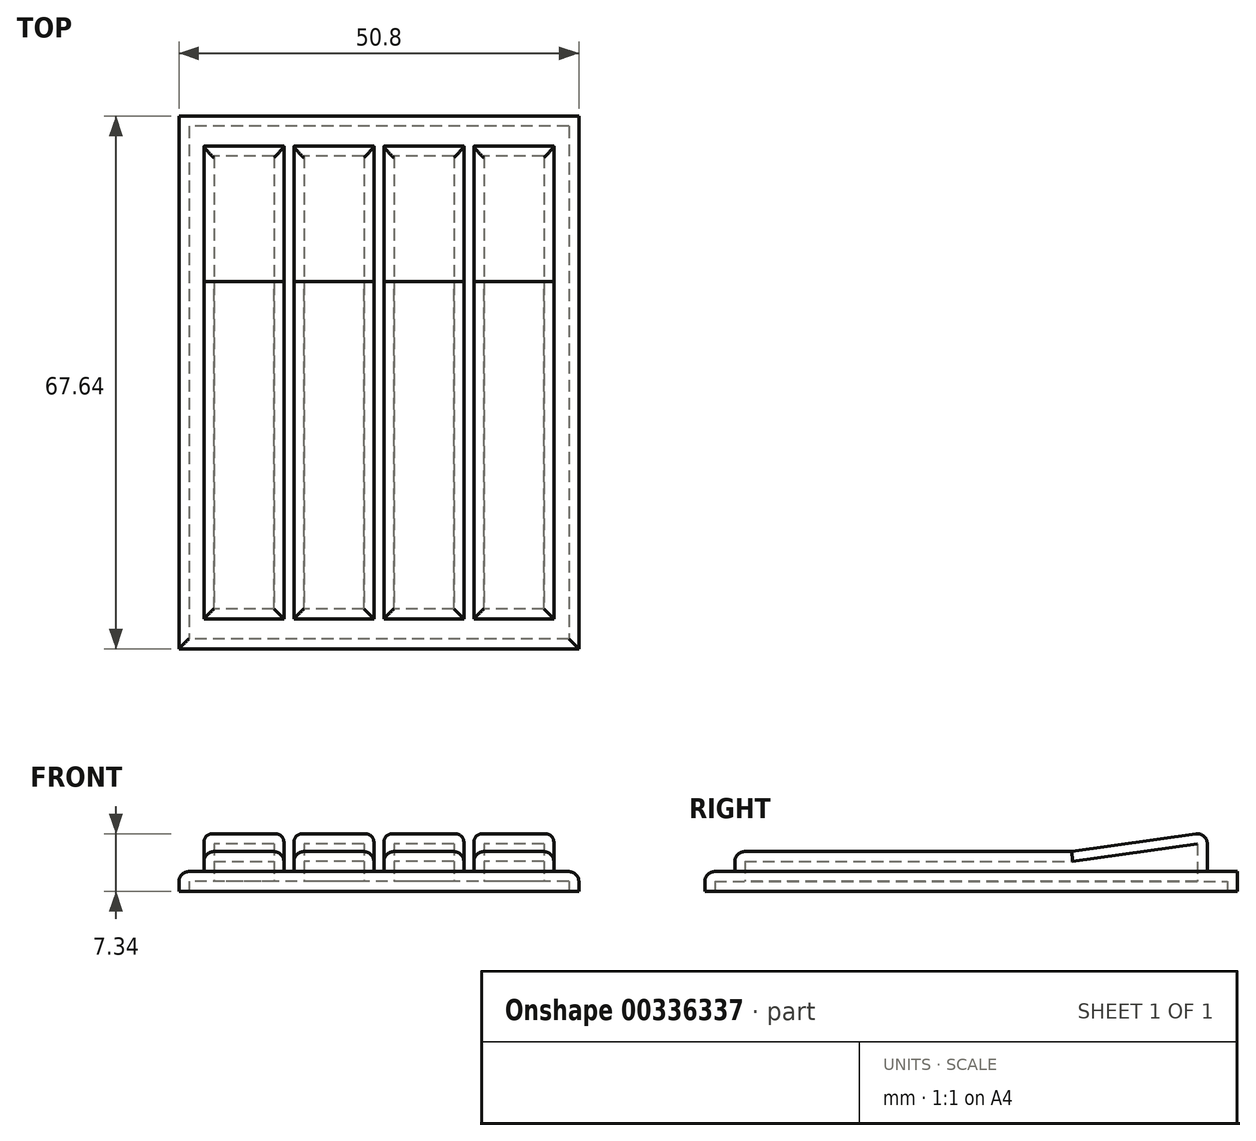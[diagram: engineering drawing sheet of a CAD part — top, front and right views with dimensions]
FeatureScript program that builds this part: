
annotation { "Feature Type Name" : "Feature", "Feature Type Description" : "" }
export const myFeature = defineFeature(function(context is Context, id is Id, definition is map)
    precondition{}
    {
        {
            var Q0;
            Q0=qCreatedBy(makeId("Top.planeOp"),FACE);
            var sketch = newSketch(context, id + "F0", { "sketchPlane" : qUnion([Q0])});
            skPoint(sketch, "E0.visualSharp", {"position": v(-51.01, 40.39) * mm});
            skPoint(sketch, "E1.visualSharp", {"position": v(51.07, 40.48) * mm});
            skPoint(sketch, "E2.visualSharp", {"position": v(0.11, -47.97) * mm});
            skLineSegment(sketch, "E3.bottom", {"start": v(25.4, 33.82) * mm, "end": v(-25.4, 33.82) * mm});
            skLineSegment(sketch, "E3.top", {"start": v(25.4, -33.82) * mm, "end": v(-25.4, -33.82) * mm});
            skLineSegment(sketch, "E3.left", {"start": v(25.4, 33.82) * mm, "end": v(25.4, -33.82) * mm});
            skLineSegment(sketch, "E3.right", {"start": v(-25.4, 33.82) * mm, "end": v(-25.4, -33.82) * mm});
            skPoint(sketch, "E3.middle", {"position": v(-17.14, 0) * mm});
            skLineSegment(sketch, "E4.bottom", {"start": v(-12.06, 30) * mm, "end": v(-22.22, 30) * mm});
            skLineSegment(sketch, "E4.top", {"start": v(-12.06, -30) * mm, "end": v(-22.22, -30) * mm});
            skLineSegment(sketch, "E4.left", {"start": v(-12.06, 30) * mm, "end": v(-12.06, -30) * mm});
            skLineSegment(sketch, "E4.right", {"start": v(-22.22, 30) * mm, "end": v(-22.22, -30) * mm});
            skPoint(sketch, "E5.1.0.0", {"position": v(-5.71, 0) * mm});
            skLineSegment(sketch, "E5.1.0.1", {"start": v(-0.63, -30) * mm, "end": v(-10.8, -30) * mm});
            skLineSegment(sketch, "E5.1.0.2", {"start": v(-0.63, 30) * mm, "end": v(-0.63, -30) * mm});
            skLineSegment(sketch, "E5.1.0.3", {"start": v(-10.8, 30) * mm, "end": v(-10.8, -30) * mm});
            skLineSegment(sketch, "E5.1.0.4", {"start": v(-0.63, 30) * mm, "end": v(-10.8, 30) * mm});
            skPoint(sketch, "E5.1.0.5", {"position": v(-5.71, 0) * mm});
            skPoint(sketch, "E5.2.0.0", {"position": v(5.72, 0) * mm});
            skLineSegment(sketch, "E5.2.0.1", {"start": v(10.8, -30) * mm, "end": v(0.64, -30) * mm});
            skLineSegment(sketch, "E5.2.0.2", {"start": v(10.8, 30) * mm, "end": v(10.8, -30) * mm});
            skLineSegment(sketch, "E5.2.0.3", {"start": v(0.64, 30) * mm, "end": v(0.64, -30) * mm});
            skLineSegment(sketch, "E5.2.0.4", {"start": v(10.8, 30) * mm, "end": v(0.64, 30) * mm});
            skPoint(sketch, "E5.2.0.5", {"position": v(5.72, 0) * mm});
            skPoint(sketch, "E5.3.0.0", {"position": v(17.15, 0) * mm});
            skLineSegment(sketch, "E5.3.0.1", {"start": v(22.23, -30) * mm, "end": v(12.07, -30) * mm});
            skLineSegment(sketch, "E5.3.0.2", {"start": v(22.23, 30) * mm, "end": v(22.23, -30) * mm});
            skLineSegment(sketch, "E5.3.0.3", {"start": v(12.07, 30) * mm, "end": v(12.07, -30) * mm});
            skLineSegment(sketch, "E5.3.0.4", {"start": v(22.23, 30) * mm, "end": v(12.07, 30) * mm});
            skPoint(sketch, "E5.3.0.5", {"position": v(17.15, 0) * mm});
            skLineSegment(sketch, "E5.direction1", {"start": v(-22.22, -30) * mm, "end": v(-10.8, -30) * mm, "construction": true});
            skLineSegment(sketch, "E6", {"start": v(-22.22, 12.8) * mm, "end": v(22.23, 12.8) * mm});
            skSolve(sketch);
        }
        {
            var Q0;
            {var subQ0=sQuery(id+"F0.wireOp",EDGE,"E4.bottom");Q0=makeQuery(id+"F0.imprint","IMPRINT",FACE,{"disambiguationData":[TD([[makeQuery(id+"F0.imprint","IMPRINT",EDGE,{"derivedFrom":subQ0}),1.0]])]});}
            var Q1;
            {var subQ0=sQuery(id+"F0.wireOp",EDGE,"E5.1.0.4");Q1=makeQuery(id+"F0.imprint","IMPRINT",FACE,{"disambiguationData":[TD([[makeQuery(id+"F0.imprint","IMPRINT",EDGE,{"derivedFrom":subQ0}),1.0]])]});}
            var Q2;
            {var subQ0=sQuery(id+"F0.wireOp",EDGE,"E5.2.0.4");Q2=makeQuery(id+"F0.imprint","IMPRINT",FACE,{"disambiguationData":[TD([[makeQuery(id+"F0.imprint","IMPRINT",EDGE,{"derivedFrom":subQ0}),1.0]])]});}
            var Q3;
            {var subQ0=sQuery(id+"F0.wireOp",EDGE,"E5.3.0.4");Q3=makeQuery(id+"F0.imprint","IMPRINT",FACE,{"disambiguationData":[TD([[makeQuery(id+"F0.imprint","IMPRINT",EDGE,{"derivedFrom":subQ0}),1.0]])]});}
            extrude(context, id + "F1", {"entities" : qUnion([Q0, Q1, Q2, Q3]), "depth" : 7.62 * mm});
        }
        {
            var Q0;
            Q0=makeQuery(id+"F0.imprint","IMPRINT",FACE,{"disambiguationData":[TD([[makeQuery(id+"F0.imprint","IMPRINT",EDGE,{"derivedFrom":sQuery(id+"F0.wireOp",EDGE,"E4.bottom")}),1.0]])]});
            var Q1;
            Q1=makeQuery(id+"F0.imprint","IMPRINT",FACE,{"disambiguationData":[TD([[makeQuery(id+"F0.imprint","IMPRINT",EDGE,{"derivedFrom":sQuery(id+"F0.wireOp",EDGE,"E5.1.0.1")}),-1.0]])]});
            var Q2;
            Q2=makeQuery(id+"F0.imprint","IMPRINT",FACE,{"disambiguationData":[TD([[makeQuery(id+"F0.imprint","IMPRINT",EDGE,{"derivedFrom":sQuery(id+"F0.wireOp",EDGE,"E5.2.0.1")}),-1.0]])]});
            var Q3;
            Q3=makeQuery(id+"F0.imprint","IMPRINT",FACE,{"disambiguationData":[TD([[makeQuery(id+"F0.imprint","IMPRINT",EDGE,{"derivedFrom":sQuery(id+"F0.wireOp",EDGE,"E5.3.0.1")}),-1.0]])]});
            var Q4;
            {var subQ0=sQuery(id+"F0.wireOp",EDGE,"E4.top");Q4=makeQuery(id+"F0.imprint","IMPRINT",FACE,{"disambiguationData":[TD([[makeQuery(id+"F0.imprint","IMPRINT",EDGE,{"derivedFrom":subQ0}),-1.0]])]});}
            var Q5;
            {var subQ0=sQuery(id+"F0.wireOp",EDGE,"E5.1.0.4");Q5=makeQuery(id+"F0.imprint","IMPRINT",FACE,{"disambiguationData":[TD([[makeQuery(id+"F0.imprint","IMPRINT",EDGE,{"derivedFrom":subQ0}),1.0]])]});}
            var Q6;
            {var subQ0=sQuery(id+"F0.wireOp",EDGE,"E5.2.0.4");Q6=makeQuery(id+"F0.imprint","IMPRINT",FACE,{"disambiguationData":[TD([[makeQuery(id+"F0.imprint","IMPRINT",EDGE,{"derivedFrom":subQ0}),1.0]])]});}
            var Q7;
            {var subQ0=sQuery(id+"F0.wireOp",EDGE,"E5.3.0.4");Q7=makeQuery(id+"F0.imprint","IMPRINT",FACE,{"disambiguationData":[TD([[makeQuery(id+"F0.imprint","IMPRINT",EDGE,{"derivedFrom":subQ0}),1.0]])]});}
            extrude(context, id + "F2", {"entities" : qUnion([Q0, Q1, Q2, Q3, Q4, Q5, Q6, Q7]), "depth" : 5.08 * mm});
        }
        {
            var Q0;
            Q0 = qSketchRegion(id + "F0", true);
            extrude(context, id + "F3", {"entities" : qUnion([Q0]), "depth" : 2.54 * mm});
        }
        {
            var Q0;
            {var subQ0=sQuery(id+"F0.wireOp",EDGE,"E6");Q0=makeQuery(id+"F1.opExtrude","CAP_EDGE",EDGE,{"disambiguationData":[OSD([subQ0]),TDD([makeQuery(id+"F0.imprint","IMPRINT",EDGE,{"disambiguationData":[TD([[makeQuery(id+"F0.imprint","INTERSECT",VERTEX,{"derivedFrom":[sQuery(id+"F0.wireOp",EDGE,"E4.right"),subQ0]}),-1.0]])],"derivedFrom":subQ0})])],"isStart":false});}
            var Q1;
            {var subQ0=sQuery(id+"F0.wireOp",EDGE,"E6");Q1=makeQuery(id+"F1.opExtrude","CAP_EDGE",EDGE,{"disambiguationData":[OSD([subQ0]),TDD([makeQuery(id+"F0.imprint","IMPRINT",EDGE,{"disambiguationData":[TD([[makeQuery(id+"F0.imprint","INTERSECT",VERTEX,{"derivedFrom":[sQuery(id+"F0.wireOp",EDGE,"E5.1.0.2"),subQ0]}),1.0]])],"derivedFrom":subQ0})])],"isStart":false});}
            var Q2;
            {var subQ0=sQuery(id+"F0.wireOp",EDGE,"E6");Q2=makeQuery(id+"F1.opExtrude","CAP_EDGE",EDGE,{"disambiguationData":[OSD([subQ0]),TDD([makeQuery(id+"F0.imprint","IMPRINT",EDGE,{"disambiguationData":[TD([[makeQuery(id+"F0.imprint","INTERSECT",VERTEX,{"derivedFrom":[sQuery(id+"F0.wireOp",EDGE,"E5.2.0.2"),subQ0]}),1.0]])],"derivedFrom":subQ0})])],"isStart":false});}
            var Q3;
            {var subQ0=sQuery(id+"F0.wireOp",EDGE,"E6");Q3=makeQuery(id+"F1.opExtrude","CAP_EDGE",EDGE,{"disambiguationData":[OSD([subQ0]),TDD([makeQuery(id+"F0.imprint","IMPRINT",EDGE,{"disambiguationData":[TD([[makeQuery(id+"F0.imprint","INTERSECT",VERTEX,{"derivedFrom":[sQuery(id+"F0.wireOp",EDGE,"E5.3.0.2"),subQ0]}),1.0]])],"derivedFrom":subQ0})])],"isStart":false});}
            chamfer(context, id + "F4", {"entities" : qUnion([Q0, Q1, Q2, Q3]), "chamferType" : ChamferType.TWO_OFFSETS, "width1" : 17.78 * mm, "oppositeDirection" : false, "width2" : 2.54 * mm, "tangentPropagation" : true});
        }
        {
            var Q0;
            Q0=makeQuery(id+"F3.opExtrude","CAP_EDGE",EDGE,{"disambiguationData":[OSD([sQuery(id+"F0.wireOp",EDGE,"E3.top")])],"isStart":false});
            var Q1;
            Q1=makeQuery(id+"F3.opExtrude","CAP_EDGE",EDGE,{"disambiguationData":[OSD([sQuery(id+"F0.wireOp",EDGE,"E3.right")])],"isStart":false});
            var Q2;
            Q2=makeQuery(id+"F3.opExtrude","CAP_EDGE",EDGE,{"disambiguationData":[OSD([sQuery(id+"F0.wireOp",EDGE,"E3.left")])],"isStart":false});
            fillet(context, id + "F5", {"entities" : qUnion([Q0, Q1, Q2]), "radius" : 1.27 * mm, "tangentPropagation" : true, "allowEdgeOverflow" : false});
        }
        {
            var Q0;
            Q0=makeQuery(id+"F2.opExtrude","CAP_FACE",FACE,{"disambiguationData":[OSD([sQuery(id+"F0.wireOp",EDGE,"E4.bottom"),sQuery(id+"F0.wireOp",EDGE,"E4.top"),sQuery(id+"F0.wireOp",EDGE,"E4.left"),sQuery(id+"F0.wireOp",EDGE,"E4.right")])],"isStart":false});
            var Q1;
            Q1=makeQuery(id+"F2.opExtrude","CAP_FACE",FACE,{"disambiguationData":[OSD([sQuery(id+"F0.wireOp",EDGE,"E5.1.0.1"),sQuery(id+"F0.wireOp",EDGE,"E5.1.0.2"),sQuery(id+"F0.wireOp",EDGE,"E5.1.0.3"),sQuery(id+"F0.wireOp",EDGE,"E5.1.0.4")])],"isStart":false});
            var Q2;
            Q2=makeQuery(id+"F2.opExtrude","CAP_FACE",FACE,{"disambiguationData":[OSD([sQuery(id+"F0.wireOp",EDGE,"E5.2.0.1"),sQuery(id+"F0.wireOp",EDGE,"E5.2.0.2"),sQuery(id+"F0.wireOp",EDGE,"E5.2.0.3"),sQuery(id+"F0.wireOp",EDGE,"E5.2.0.4")])],"isStart":false});
            var Q3;
            Q3=makeQuery(id+"F2.opExtrude","CAP_FACE",FACE,{"disambiguationData":[OSD([sQuery(id+"F0.wireOp",EDGE,"E5.3.0.1"),sQuery(id+"F0.wireOp",EDGE,"E5.3.0.2"),sQuery(id+"F0.wireOp",EDGE,"E5.3.0.3"),sQuery(id+"F0.wireOp",EDGE,"E5.3.0.4")])],"isStart":false});
            fillet(context, id + "F6", {"entities" : qUnion([Q0, Q1, Q2, Q3]), "radius" : 1.27 * mm, "tangentPropagation" : true, "allowEdgeOverflow" : false});
        }
        {
            var Q0;
            {var subQ0=sQuery(id+"F0.wireOp",EDGE,"E6");Q0=makeQuery(id+"F4.opChamfer","BLEND_EDGE",EDGE,{"blendedFrom":[makeQuery(id+"F1.opExtrude","CAP_EDGE",EDGE,{"disambiguationData":[OSD([subQ0]),TDD([makeQuery(id+"F0.imprint","IMPRINT",EDGE,{"disambiguationData":[TD([[makeQuery(id+"F0.imprint","INTERSECT",VERTEX,{"derivedFrom":[sQuery(id+"F0.wireOp",EDGE,"E4.right"),subQ0]}),-1.0]])],"derivedFrom":subQ0})])],"isStart":false}),makeQuery(id+"F1.opExtrude","SWEPT_FACE",FACE,{"disambiguationData":[OSD([sQuery(id+"F0.wireOp",EDGE,"E4.bottom")])]})],"blendedInto":[makeQuery(id+"F1.opExtrude","SWEPT_FACE",FACE,{"disambiguationData":[OSD([sQuery(id+"F0.wireOp",EDGE,"E4.bottom")])]})]});}
            var Q1;
            {var subQ0=sQuery(id+"F0.wireOp",EDGE,"E4.right");var subQ1=sQuery(id+"F0.wireOp",EDGE,"E6");Q1=makeQuery(id+"F4.opChamfer","BLEND_EDGE",EDGE,{"blendedFrom":[makeQuery(id+"F1.opExtrude","CAP_EDGE",EDGE,{"disambiguationData":[OSD([subQ1]),TDD([makeQuery(id+"F0.imprint","IMPRINT",EDGE,{"disambiguationData":[TD([[makeQuery(id+"F0.imprint","INTERSECT",VERTEX,{"derivedFrom":[subQ0,subQ1]}),-1.0]])],"derivedFrom":subQ1})])],"isStart":false}),makeQuery(id+"F1.opExtrude","SWEPT_FACE",FACE,{"disambiguationData":[OSD([subQ0])]})],"blendedInto":[makeQuery(id+"F1.opExtrude","SWEPT_FACE",FACE,{"disambiguationData":[OSD([subQ0])]})]});}
            var Q2;
            {var subQ0=sQuery(id+"F0.wireOp",EDGE,"E4.left");var subQ1=sQuery(id+"F0.wireOp",EDGE,"E6");Q2=makeQuery(id+"F4.opChamfer","BLEND_EDGE",EDGE,{"blendedFrom":[makeQuery(id+"F1.opExtrude","CAP_EDGE",EDGE,{"disambiguationData":[OSD([subQ1]),TDD([makeQuery(id+"F0.imprint","IMPRINT",EDGE,{"disambiguationData":[TD([[makeQuery(id+"F0.imprint","INTERSECT",VERTEX,{"derivedFrom":[sQuery(id+"F0.wireOp",EDGE,"E4.right"),subQ1]}),-1.0]])],"derivedFrom":subQ1})])],"isStart":false}),makeQuery(id+"F1.opExtrude","SWEPT_FACE",FACE,{"disambiguationData":[OSD([subQ0])]})],"blendedInto":[makeQuery(id+"F1.opExtrude","SWEPT_FACE",FACE,{"disambiguationData":[OSD([subQ0])]})]});}
            var Q3;
            {var subQ0=sQuery(id+"F0.wireOp",EDGE,"E5.1.0.3");var subQ1=sQuery(id+"F0.wireOp",EDGE,"E6");Q3=makeQuery(id+"F4.opChamfer","BLEND_EDGE",EDGE,{"blendedFrom":[makeQuery(id+"F1.opExtrude","CAP_EDGE",EDGE,{"disambiguationData":[OSD([subQ1]),TDD([makeQuery(id+"F0.imprint","IMPRINT",EDGE,{"disambiguationData":[TD([[makeQuery(id+"F0.imprint","INTERSECT",VERTEX,{"derivedFrom":[sQuery(id+"F0.wireOp",EDGE,"E5.1.0.2"),subQ1]}),1.0]])],"derivedFrom":subQ1})])],"isStart":false}),makeQuery(id+"F1.opExtrude","SWEPT_FACE",FACE,{"disambiguationData":[OSD([subQ0])]})],"blendedInto":[makeQuery(id+"F1.opExtrude","SWEPT_FACE",FACE,{"disambiguationData":[OSD([subQ0])]})]});}
            var Q4;
            {var subQ0=sQuery(id+"F0.wireOp",EDGE,"E6");Q4=makeQuery(id+"F4.opChamfer","BLEND_EDGE",EDGE,{"blendedFrom":[makeQuery(id+"F1.opExtrude","CAP_EDGE",EDGE,{"disambiguationData":[OSD([subQ0]),TDD([makeQuery(id+"F0.imprint","IMPRINT",EDGE,{"disambiguationData":[TD([[makeQuery(id+"F0.imprint","INTERSECT",VERTEX,{"derivedFrom":[sQuery(id+"F0.wireOp",EDGE,"E5.1.0.2"),subQ0]}),1.0]])],"derivedFrom":subQ0})])],"isStart":false}),makeQuery(id+"F1.opExtrude","SWEPT_FACE",FACE,{"disambiguationData":[OSD([sQuery(id+"F0.wireOp",EDGE,"E5.1.0.4")])]})],"blendedInto":[makeQuery(id+"F1.opExtrude","SWEPT_FACE",FACE,{"disambiguationData":[OSD([sQuery(id+"F0.wireOp",EDGE,"E5.1.0.4")])]})]});}
            var Q5;
            {var subQ0=sQuery(id+"F0.wireOp",EDGE,"E5.1.0.2");var subQ1=sQuery(id+"F0.wireOp",EDGE,"E6");Q5=makeQuery(id+"F4.opChamfer","BLEND_EDGE",EDGE,{"blendedFrom":[makeQuery(id+"F1.opExtrude","CAP_EDGE",EDGE,{"disambiguationData":[OSD([subQ1]),TDD([makeQuery(id+"F0.imprint","IMPRINT",EDGE,{"disambiguationData":[TD([[makeQuery(id+"F0.imprint","INTERSECT",VERTEX,{"derivedFrom":[subQ0,subQ1]}),1.0]])],"derivedFrom":subQ1})])],"isStart":false}),makeQuery(id+"F1.opExtrude","SWEPT_FACE",FACE,{"disambiguationData":[OSD([subQ0])]})],"blendedInto":[makeQuery(id+"F1.opExtrude","SWEPT_FACE",FACE,{"disambiguationData":[OSD([subQ0])]})]});}
            var Q6;
            {var subQ0=sQuery(id+"F0.wireOp",EDGE,"E5.2.0.3");var subQ1=sQuery(id+"F0.wireOp",EDGE,"E6");Q6=makeQuery(id+"F4.opChamfer","BLEND_EDGE",EDGE,{"blendedFrom":[makeQuery(id+"F1.opExtrude","CAP_EDGE",EDGE,{"disambiguationData":[OSD([subQ1]),TDD([makeQuery(id+"F0.imprint","IMPRINT",EDGE,{"disambiguationData":[TD([[makeQuery(id+"F0.imprint","INTERSECT",VERTEX,{"derivedFrom":[sQuery(id+"F0.wireOp",EDGE,"E5.2.0.2"),subQ1]}),1.0]])],"derivedFrom":subQ1})])],"isStart":false}),makeQuery(id+"F1.opExtrude","SWEPT_FACE",FACE,{"disambiguationData":[OSD([subQ0])]})],"blendedInto":[makeQuery(id+"F1.opExtrude","SWEPT_FACE",FACE,{"disambiguationData":[OSD([subQ0])]})]});}
            var Q7;
            {var subQ0=sQuery(id+"F0.wireOp",EDGE,"E6");Q7=makeQuery(id+"F4.opChamfer","BLEND_EDGE",EDGE,{"blendedFrom":[makeQuery(id+"F1.opExtrude","CAP_EDGE",EDGE,{"disambiguationData":[OSD([subQ0]),TDD([makeQuery(id+"F0.imprint","IMPRINT",EDGE,{"disambiguationData":[TD([[makeQuery(id+"F0.imprint","INTERSECT",VERTEX,{"derivedFrom":[sQuery(id+"F0.wireOp",EDGE,"E5.2.0.2"),subQ0]}),1.0]])],"derivedFrom":subQ0})])],"isStart":false}),makeQuery(id+"F1.opExtrude","SWEPT_FACE",FACE,{"disambiguationData":[OSD([sQuery(id+"F0.wireOp",EDGE,"E5.2.0.4")])]})],"blendedInto":[makeQuery(id+"F1.opExtrude","SWEPT_FACE",FACE,{"disambiguationData":[OSD([sQuery(id+"F0.wireOp",EDGE,"E5.2.0.4")])]})]});}
            var Q8;
            {var subQ0=sQuery(id+"F0.wireOp",EDGE,"E5.2.0.2");var subQ1=sQuery(id+"F0.wireOp",EDGE,"E6");Q8=makeQuery(id+"F4.opChamfer","BLEND_EDGE",EDGE,{"blendedFrom":[makeQuery(id+"F1.opExtrude","CAP_EDGE",EDGE,{"disambiguationData":[OSD([subQ1]),TDD([makeQuery(id+"F0.imprint","IMPRINT",EDGE,{"disambiguationData":[TD([[makeQuery(id+"F0.imprint","INTERSECT",VERTEX,{"derivedFrom":[subQ0,subQ1]}),1.0]])],"derivedFrom":subQ1})])],"isStart":false}),makeQuery(id+"F1.opExtrude","SWEPT_FACE",FACE,{"disambiguationData":[OSD([subQ0])]})],"blendedInto":[makeQuery(id+"F1.opExtrude","SWEPT_FACE",FACE,{"disambiguationData":[OSD([subQ0])]})]});}
            var Q9;
            {var subQ0=sQuery(id+"F0.wireOp",EDGE,"E5.3.0.3");var subQ1=sQuery(id+"F0.wireOp",EDGE,"E6");Q9=makeQuery(id+"F4.opChamfer","BLEND_EDGE",EDGE,{"blendedFrom":[makeQuery(id+"F1.opExtrude","CAP_EDGE",EDGE,{"disambiguationData":[OSD([subQ1]),TDD([makeQuery(id+"F0.imprint","IMPRINT",EDGE,{"disambiguationData":[TD([[makeQuery(id+"F0.imprint","INTERSECT",VERTEX,{"derivedFrom":[sQuery(id+"F0.wireOp",EDGE,"E5.3.0.2"),subQ1]}),1.0]])],"derivedFrom":subQ1})])],"isStart":false}),makeQuery(id+"F1.opExtrude","SWEPT_FACE",FACE,{"disambiguationData":[OSD([subQ0])]})],"blendedInto":[makeQuery(id+"F1.opExtrude","SWEPT_FACE",FACE,{"disambiguationData":[OSD([subQ0])]})]});}
            var Q10;
            {var subQ0=sQuery(id+"F0.wireOp",EDGE,"E6");Q10=makeQuery(id+"F4.opChamfer","BLEND_EDGE",EDGE,{"blendedFrom":[makeQuery(id+"F1.opExtrude","CAP_EDGE",EDGE,{"disambiguationData":[OSD([subQ0]),TDD([makeQuery(id+"F0.imprint","IMPRINT",EDGE,{"disambiguationData":[TD([[makeQuery(id+"F0.imprint","INTERSECT",VERTEX,{"derivedFrom":[sQuery(id+"F0.wireOp",EDGE,"E5.3.0.2"),subQ0]}),1.0]])],"derivedFrom":subQ0})])],"isStart":false}),makeQuery(id+"F1.opExtrude","SWEPT_FACE",FACE,{"disambiguationData":[OSD([sQuery(id+"F0.wireOp",EDGE,"E5.3.0.4")])]})],"blendedInto":[makeQuery(id+"F1.opExtrude","SWEPT_FACE",FACE,{"disambiguationData":[OSD([sQuery(id+"F0.wireOp",EDGE,"E5.3.0.4")])]})]});}
            var Q11;
            {var subQ0=sQuery(id+"F0.wireOp",EDGE,"E5.3.0.2");var subQ1=sQuery(id+"F0.wireOp",EDGE,"E6");Q11=makeQuery(id+"F4.opChamfer","BLEND_EDGE",EDGE,{"blendedFrom":[makeQuery(id+"F1.opExtrude","CAP_EDGE",EDGE,{"disambiguationData":[OSD([subQ1]),TDD([makeQuery(id+"F0.imprint","IMPRINT",EDGE,{"disambiguationData":[TD([[makeQuery(id+"F0.imprint","INTERSECT",VERTEX,{"derivedFrom":[subQ0,subQ1]}),1.0]])],"derivedFrom":subQ1})])],"isStart":false}),makeQuery(id+"F1.opExtrude","SWEPT_FACE",FACE,{"disambiguationData":[OSD([subQ0])]})],"blendedInto":[makeQuery(id+"F1.opExtrude","SWEPT_FACE",FACE,{"disambiguationData":[OSD([subQ0])]})]});}
            fillet(context, id + "F7", {"entities" : qUnion([Q0, Q1, Q2, Q3, Q4, Q5, Q6, Q7, Q8, Q9, Q10, Q11]), "radius" : 1.27 * mm, "tangentPropagation" : true, "allowEdgeOverflow" : false});
        }
        {
            var Q0;
            Q0=makeQuery(id+"F1.opExtrude","SWEPT_BODY",BODY,{"disambiguationData":[OSD([sQuery(id+"F0.wireOp",EDGE,"E5.2.0.2"),sQuery(id+"F0.wireOp",EDGE,"E5.2.0.3"),sQuery(id+"F0.wireOp",EDGE,"E5.2.0.4"),sQuery(id+"F0.wireOp",EDGE,"E6")])]});
            var Q1;
            Q1=makeQuery(id+"F2.opExtrude","SWEPT_BODY",BODY,{"disambiguationData":[OSD([sQuery(id+"F0.wireOp",EDGE,"E5.3.0.1"),sQuery(id+"F0.wireOp",EDGE,"E5.3.0.2"),sQuery(id+"F0.wireOp",EDGE,"E5.3.0.3"),sQuery(id+"F0.wireOp",EDGE,"E5.3.0.4")])]});
            var Q2;
            Q2=makeQuery(id+"F3.opExtrude","SWEPT_BODY",BODY,{"disambiguationData":[OSD([sQuery(id+"F0.wireOp",EDGE,"E3.bottom"),sQuery(id+"F0.wireOp",EDGE,"E3.top"),sQuery(id+"F0.wireOp",EDGE,"E3.left"),sQuery(id+"F0.wireOp",EDGE,"E3.right"),sQuery(id+"F0.wireOp",EDGE,"E4.bottom"),sQuery(id+"F0.wireOp",EDGE,"E4.top"),sQuery(id+"F0.wireOp",EDGE,"E4.left"),sQuery(id+"F0.wireOp",EDGE,"E4.right"),sQuery(id+"F0.wireOp",EDGE,"E5.1.0.1"),sQuery(id+"F0.wireOp",EDGE,"E5.1.0.2"),sQuery(id+"F0.wireOp",EDGE,"E5.1.0.3"),sQuery(id+"F0.wireOp",EDGE,"E5.1.0.4"),sQuery(id+"F0.wireOp",EDGE,"E5.2.0.1"),sQuery(id+"F0.wireOp",EDGE,"E5.2.0.2"),sQuery(id+"F0.wireOp",EDGE,"E5.2.0.3"),sQuery(id+"F0.wireOp",EDGE,"E5.2.0.4"),sQuery(id+"F0.wireOp",EDGE,"E5.3.0.1"),sQuery(id+"F0.wireOp",EDGE,"E5.3.0.2"),sQuery(id+"F0.wireOp",EDGE,"E5.3.0.3"),sQuery(id+"F0.wireOp",EDGE,"E5.3.0.4")])]});
            var Q3;
            Q3=makeQuery(id+"F2.opExtrude","SWEPT_BODY",BODY,{"disambiguationData":[OSD([sQuery(id+"F0.wireOp",EDGE,"E5.2.0.1"),sQuery(id+"F0.wireOp",EDGE,"E5.2.0.2"),sQuery(id+"F0.wireOp",EDGE,"E5.2.0.3"),sQuery(id+"F0.wireOp",EDGE,"E5.2.0.4")])]});
            var Q4;
            Q4=makeQuery(id+"F1.opExtrude","SWEPT_BODY",BODY,{"disambiguationData":[OSD([sQuery(id+"F0.wireOp",EDGE,"E5.3.0.2"),sQuery(id+"F0.wireOp",EDGE,"E5.3.0.3"),sQuery(id+"F0.wireOp",EDGE,"E5.3.0.4"),sQuery(id+"F0.wireOp",EDGE,"E6")])]});
            var Q5;
            Q5=makeQuery(id+"F1.opExtrude","SWEPT_BODY",BODY,{"disambiguationData":[OSD([sQuery(id+"F0.wireOp",EDGE,"E5.1.0.2"),sQuery(id+"F0.wireOp",EDGE,"E5.1.0.3"),sQuery(id+"F0.wireOp",EDGE,"E5.1.0.4"),sQuery(id+"F0.wireOp",EDGE,"E6")])]});
            var Q6;
            Q6=makeQuery(id+"F1.opExtrude","SWEPT_BODY",BODY,{"disambiguationData":[OSD([sQuery(id+"F0.wireOp",EDGE,"E4.bottom"),sQuery(id+"F0.wireOp",EDGE,"E4.left"),sQuery(id+"F0.wireOp",EDGE,"E4.right"),sQuery(id+"F0.wireOp",EDGE,"E6")])]});
            var Q7;
            Q7=makeQuery(id+"F2.opExtrude","SWEPT_BODY",BODY,{"disambiguationData":[OSD([sQuery(id+"F0.wireOp",EDGE,"E4.bottom"),sQuery(id+"F0.wireOp",EDGE,"E4.top"),sQuery(id+"F0.wireOp",EDGE,"E4.left"),sQuery(id+"F0.wireOp",EDGE,"E4.right")])]});
            var Q8;
            Q8=makeQuery(id+"F2.opExtrude","SWEPT_BODY",BODY,{"disambiguationData":[OSD([sQuery(id+"F0.wireOp",EDGE,"E5.1.0.1"),sQuery(id+"F0.wireOp",EDGE,"E5.1.0.2"),sQuery(id+"F0.wireOp",EDGE,"E5.1.0.3"),sQuery(id+"F0.wireOp",EDGE,"E5.1.0.4")])]});
            booleanBodies(context, id + "F8", {"operationType" : BooleanOperationType.UNION, "tools" : qUnion([Q0, Q1, Q2, Q3, Q4, Q5, Q6, Q7, Q8])});
        }
        {
            var Q0;
            {var subQ0=sQuery(id+"F0.wireOp",EDGE,"E5.3.0.4");var subQ1=sQuery(id+"F0.wireOp",EDGE,"E5.3.0.3");var subQ2=sQuery(id+"F0.wireOp",EDGE,"E5.3.0.2");var subQ3=sQuery(id+"F0.wireOp",EDGE,"E5.3.0.1");var subQ4=sQuery(id+"F0.wireOp",EDGE,"E5.2.0.4");var subQ5=sQuery(id+"F0.wireOp",EDGE,"E5.2.0.3");var subQ6=sQuery(id+"F0.wireOp",EDGE,"E5.2.0.2");var subQ7=sQuery(id+"F0.wireOp",EDGE,"E5.2.0.1");var subQ8=sQuery(id+"F0.wireOp",EDGE,"E5.1.0.4");var subQ9=sQuery(id+"F0.wireOp",EDGE,"E5.1.0.3");var subQ10=sQuery(id+"F0.wireOp",EDGE,"E5.1.0.2");var subQ11=sQuery(id+"F0.wireOp",EDGE,"E5.1.0.1");var subQ12=sQuery(id+"F0.wireOp",EDGE,"E4.right");var subQ13=sQuery(id+"F0.wireOp",EDGE,"E4.left");var subQ14=sQuery(id+"F0.wireOp",EDGE,"E4.top");var subQ15=sQuery(id+"F0.wireOp",EDGE,"E4.bottom");var subQ16=sQuery(id+"F0.wireOp",EDGE,"E6");Q0=makeQuery(id+"F8.opBoolean","MERGE",FACE,{"derivedFrom":[makeQuery(id+"F1.opExtrude","CAP_FACE",FACE,{"disambiguationData":[OSD([subQ15,subQ13,subQ12,subQ16])],"isStart":true}),makeQuery(id+"F1.opExtrude","CAP_FACE",FACE,{"disambiguationData":[OSD([subQ10,subQ9,subQ8,subQ16])],"isStart":true}),makeQuery(id+"F1.opExtrude","CAP_FACE",FACE,{"disambiguationData":[OSD([subQ6,subQ5,subQ4,subQ16])],"isStart":true}),makeQuery(id+"F1.opExtrude","CAP_FACE",FACE,{"disambiguationData":[OSD([subQ2,subQ1,subQ0,subQ16])],"isStart":true}),makeQuery(id+"F2.opExtrude","CAP_FACE",FACE,{"disambiguationData":[OSD([subQ15,subQ14,subQ13,subQ12])],"isStart":true}),makeQuery(id+"F2.opExtrude","CAP_FACE",FACE,{"disambiguationData":[OSD([subQ11,subQ10,subQ9,subQ8])],"isStart":true}),makeQuery(id+"F2.opExtrude","CAP_FACE",FACE,{"disambiguationData":[OSD([subQ7,subQ6,subQ5,subQ4])],"isStart":true}),makeQuery(id+"F2.opExtrude","CAP_FACE",FACE,{"disambiguationData":[OSD([subQ3,subQ2,subQ1,subQ0])],"isStart":true}),makeQuery(id+"F3.opExtrude","CAP_FACE",FACE,{"disambiguationData":[OSD([sQuery(id+"F0.wireOp",EDGE,"E3.bottom"),sQuery(id+"F0.wireOp",EDGE,"E3.top"),sQuery(id+"F0.wireOp",EDGE,"E3.left"),sQuery(id+"F0.wireOp",EDGE,"E3.right"),subQ15,subQ14,subQ13,subQ12,subQ11,subQ10,subQ9,subQ8,subQ7,subQ6,subQ5,subQ4,subQ3,subQ2,subQ1,subQ0])],"isStart":true})]});}
            shell(context, id + "F9", {"entities" : qUnion([Q0]), "thickness" : 1.27 * mm});
        }
    });
